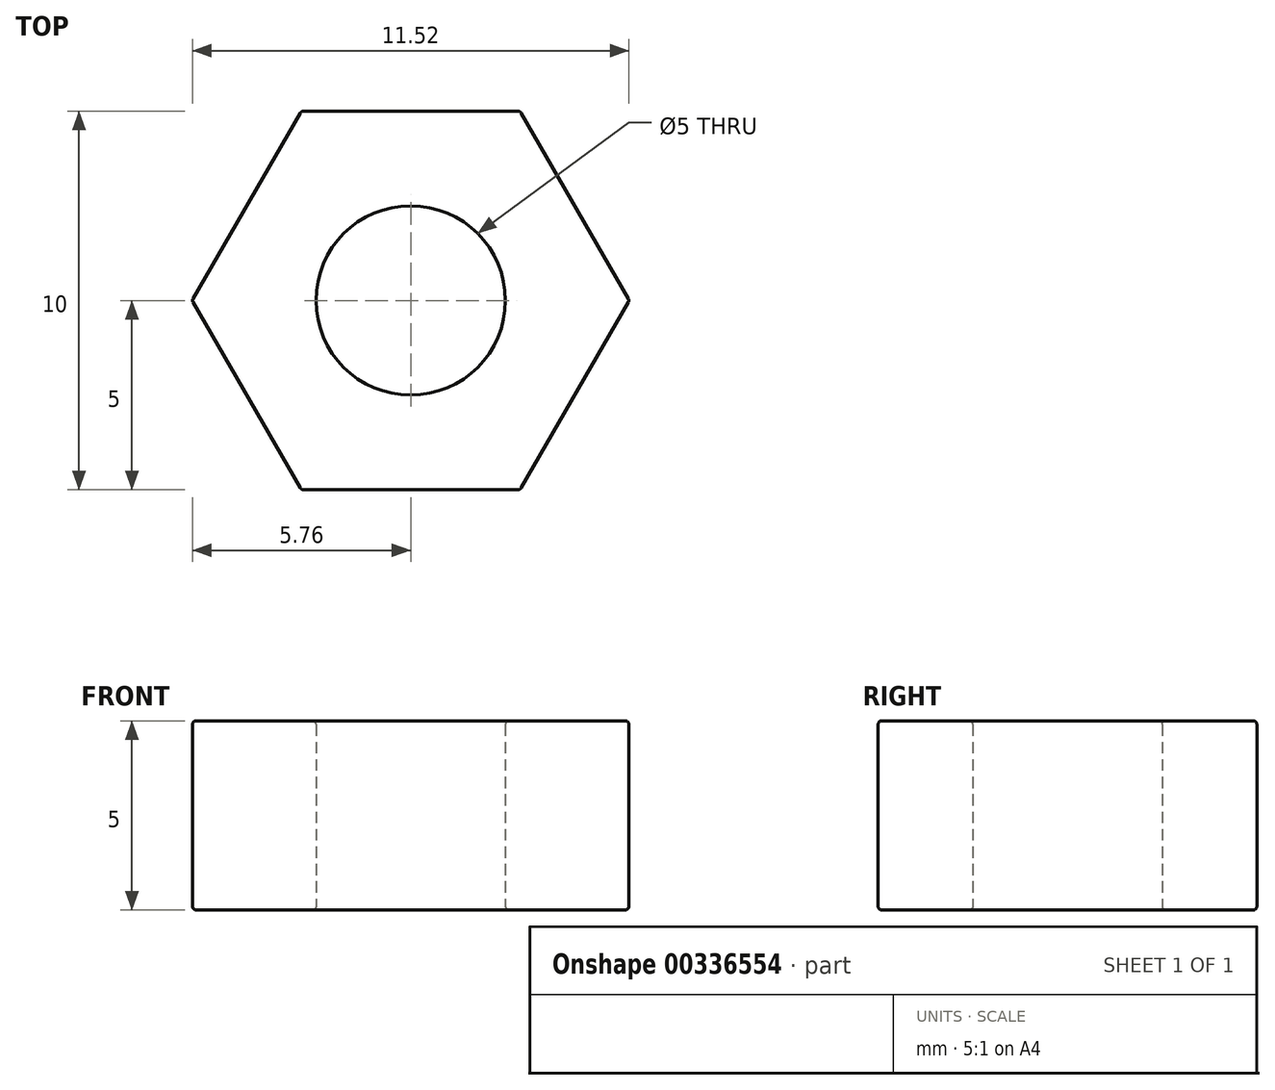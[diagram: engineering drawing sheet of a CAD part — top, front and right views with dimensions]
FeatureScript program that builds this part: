
annotation { "Feature Type Name" : "Feature", "Feature Type Description" : "" }
export const myFeature = defineFeature(function(context is Context, id is Id, definition is map)
    precondition{}
    {
        {
            var Q0;
            Q0=qCreatedBy(makeId("Top.planeOp"),FACE);
            var sketch = newSketch(context, id + "F0", { "sketchPlane" : qUnion([Q0])});
            skCircle(sketch, "E0.cCircle", {"center": v(0, 0) * mm, "radius": 5 * mm, "construction": true});
            skLineSegment(sketch, "E0.0", {"start": v(2.89, 5) * mm, "end": v(5.77, 0) * mm});
            skLineSegment(sketch, "E0.1", {"start": v(5.77, 0) * mm, "end": v(2.89, -5) * mm});
            skLineSegment(sketch, "E0.2", {"start": v(2.89, -5) * mm, "end": v(-2.89, -5) * mm});
            skLineSegment(sketch, "E0.3", {"start": v(-2.89, -5) * mm, "end": v(-5.77, 0) * mm});
            skLineSegment(sketch, "E0.4", {"start": v(-5.77, 0) * mm, "end": v(-2.89, 5) * mm});
            skLineSegment(sketch, "E0.5", {"start": v(-2.89, 5) * mm, "end": v(2.89, 5) * mm});
            skPoint(sketch, "E0.0.midPoint", {"position": v(4.33, 2.5) * mm});
            skCircle(sketch, "E1", {"center": v(0, 0) * mm, "radius": 2.5 * mm});
            skSolve(sketch);
        }
        {
            var Q0;
            Q0 = qSketchRegion(id + "F0", true);
            extrude(context, id + "F1", {"entities" : qUnion([Q0]), "depth" : 5 * mm});
        }
        {
            var Q0;
            Q0=makeQuery(id+"F1.opExtrude","SWEPT_FACE",FACE,{"disambiguationData":[OSD([sQuery(id+"F0.wireOp",EDGE,"E0.1")])]});
            var Q1;
            Q1=makeQuery(id+"F1.opExtrude","SWEPT_FACE",FACE,{"disambiguationData":[OSD([sQuery(id+"F0.wireOp",EDGE,"E0.2")])]});
            var Q2;
            Q2=makeQuery(id+"F1.opExtrude","CAP_FACE",FACE,{"disambiguationData":[OSD([sQuery(id+"F0.wireOp",EDGE,"E0.0"),sQuery(id+"F0.wireOp",EDGE,"E0.1"),sQuery(id+"F0.wireOp",EDGE,"E0.2"),sQuery(id+"F0.wireOp",EDGE,"E0.3"),sQuery(id+"F0.wireOp",EDGE,"E0.4"),sQuery(id+"F0.wireOp",EDGE,"E0.5"),sQuery(id+"F0.wireOp",EDGE,"E1")])],"isStart":false});
            var Q3;
            Q3=makeQuery(id+"F1.opExtrude","SWEPT_FACE",FACE,{"disambiguationData":[OSD([sQuery(id+"F0.wireOp",EDGE,"E0.0")])]});
            var Q4;
            Q4=makeQuery(id+"F1.opExtrude","SWEPT_FACE",FACE,{"disambiguationData":[OSD([sQuery(id+"F0.wireOp",EDGE,"E0.3")])]});
            var Q5;
            Q5=makeQuery(id+"F1.opExtrude","SWEPT_FACE",FACE,{"disambiguationData":[OSD([sQuery(id+"F0.wireOp",EDGE,"E0.4")])]});
            var Q6;
            Q6=makeQuery(id+"F1.opExtrude","SWEPT_FACE",FACE,{"disambiguationData":[OSD([sQuery(id+"F0.wireOp",EDGE,"E0.5")])]});
            var Q7;
            Q7=makeQuery(id+"F1.opExtrude","CAP_FACE",FACE,{"disambiguationData":[OSD([sQuery(id+"F0.wireOp",EDGE,"E0.0"),sQuery(id+"F0.wireOp",EDGE,"E0.1"),sQuery(id+"F0.wireOp",EDGE,"E0.2"),sQuery(id+"F0.wireOp",EDGE,"E0.3"),sQuery(id+"F0.wireOp",EDGE,"E0.4"),sQuery(id+"F0.wireOp",EDGE,"E0.5"),sQuery(id+"F0.wireOp",EDGE,"E1")])],"isStart":true});
            fillet(context, id + "F2", {"entities" : qUnion([Q0, Q1, Q2, Q3, Q4, Q5, Q6, Q7]), "radius" : 0.1 * mm, "tangentPropagation" : true, "allowEdgeOverflow" : false});
        }
    });
